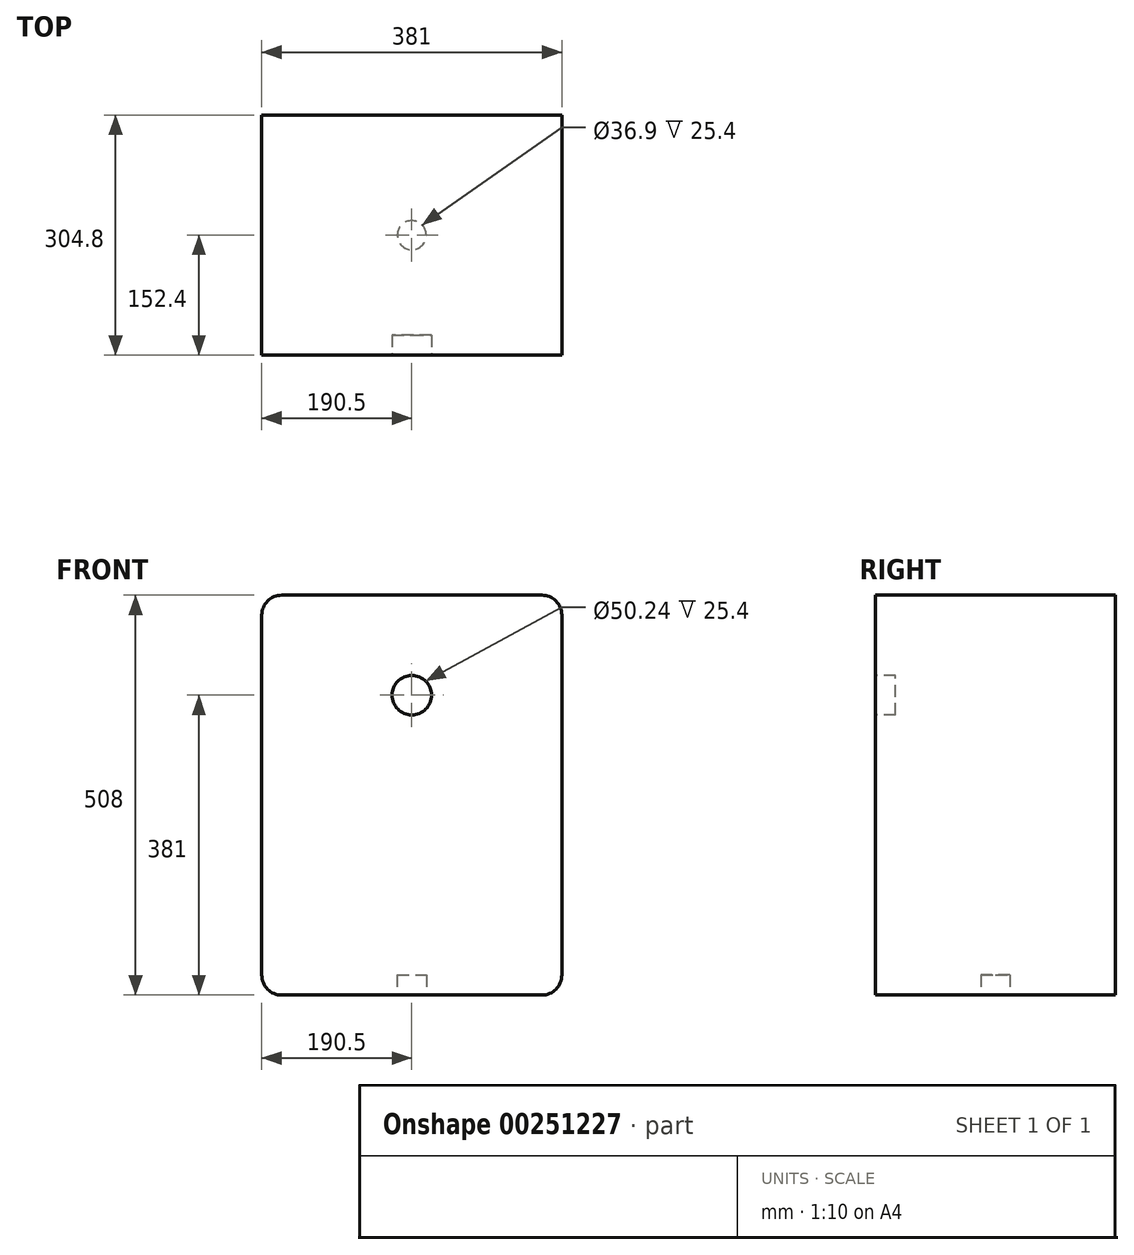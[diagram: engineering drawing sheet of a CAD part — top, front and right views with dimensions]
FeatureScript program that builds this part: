
annotation { "Feature Type Name" : "Feature", "Feature Type Description" : "" }
export const myFeature = defineFeature(function(context is Context, id is Id, definition is map)
    precondition{}
    {
        {
            var Q0;
            Q0=qCreatedBy(makeId("Front.planeOp"),FACE);
            var sketch = newSketch(context, id + "F0", { "sketchPlane" : qUnion([Q0])});
            skLineSegment(sketch, "E0.bottom", {"start": v(-190.5, 254) * mm, "end": v(190.5, 254) * mm});
            skLineSegment(sketch, "E0.top", {"start": v(-190.5, -254) * mm, "end": v(190.5, -254) * mm});
            skLineSegment(sketch, "E0.left", {"start": v(-190.5, 254) * mm, "end": v(-190.5, -254) * mm});
            skLineSegment(sketch, "E0.right", {"start": v(190.5, 254) * mm, "end": v(190.5, -254) * mm});
            skPoint(sketch, "E0.middle", {"position": v(0, 0) * mm});
            skSolve(sketch);
        }
        {
            var Q0;
            Q0=makeQuery(id+"F0.imprint","IMPRINT",FACE,{"disambiguationData":[TD([[makeQuery(id+"F0.imprint","IMPRINT",EDGE,{"derivedFrom":sQuery(id+"F0.wireOp",EDGE,"E0.bottom")}),-1.0]])]});
            extrude(context, id + "F1", {"entities" : qUnion([Q0]), "depth" : 304.8 * mm});
        }
        {
            var Q0;
            Q0=makeQuery(id+"F1.opExtrude","SWEPT_EDGE",EDGE,{"disambiguationData":[OSD([sQuery(id+"F0.wireOp",EDGE,"E0.bottom"),sQuery(id+"F0.wireOp",EDGE,"E0.left")])]});
            var Q1;
            Q1=makeQuery(id+"F1.opExtrude","SWEPT_EDGE",EDGE,{"disambiguationData":[OSD([sQuery(id+"F0.wireOp",EDGE,"E0.bottom"),sQuery(id+"F0.wireOp",EDGE,"E0.right")])]});
            var Q2;
            Q2=makeQuery(id+"F1.opExtrude","SWEPT_EDGE",EDGE,{"disambiguationData":[OSD([sQuery(id+"F0.wireOp",EDGE,"E0.top"),sQuery(id+"F0.wireOp",EDGE,"E0.right")])]});
            var Q3;
            Q3=makeQuery(id+"F1.opExtrude","SWEPT_EDGE",EDGE,{"disambiguationData":[OSD([sQuery(id+"F0.wireOp",EDGE,"E0.top"),sQuery(id+"F0.wireOp",EDGE,"E0.left")])]});
            fillet(context, id + "F2", {"entities" : qUnion([Q0, Q1, Q2, Q3]), "radius" : 25.4 * mm, "tangentPropagation" : true, "allowEdgeOverflow" : false});
        }
        {
            var Q0;
            Q0=makeQuery(id+"F1.opExtrude","SWEPT_FACE",FACE,{"disambiguationData":[OSD([sQuery(id+"F0.wireOp",EDGE,"E0.top")])]});
            var sketch = newSketch(context, id + "F3", { "sketchPlane" : qUnion([Q0])});
            skCircle(sketch, "E1", {"center": v(0, 152.4) * mm, "radius": 18.45 * mm});
            skPoint(sketch, "E1.centerSnap0", {"position": v(-165.1, 152.4) * mm});
            skPoint(sketch, "E1.centerSnap1", {"position": v(0, 304.8) * mm});
            skSolve(sketch);
        }
        {
            var Q0;
            Q0=makeQuery(id+"F3.imprint","IMPRINT",FACE,{"disambiguationData":[TD([[makeQuery(id+"F3.imprint","IMPRINT",EDGE,{"derivedFrom":sQuery(id+"F3.wireOp",EDGE,"E1")}),1.0]])]});
            extrude(context, id + "F4", {"entities" : qUnion([Q0]), "operationType" : NewBodyOperationType.REMOVE, "oppositeDirection" : true, "depth" : 25.4 * mm});
        }
        {
            var Q0;
            Q0=makeQuery(id+"F1.opExtrude","CAP_FACE",FACE,{"disambiguationData":[OSD([sQuery(id+"F0.wireOp",EDGE,"E0.bottom"),sQuery(id+"F0.wireOp",EDGE,"E0.top"),sQuery(id+"F0.wireOp",EDGE,"E0.left"),sQuery(id+"F0.wireOp",EDGE,"E0.right")])],"isStart":false});
            var sketch = newSketch(context, id + "F5", { "sketchPlane" : qUnion([Q0])});
            skSolve(sketch);
        }
        {
            var Q0;
            {var subQ3=sQuery(id+"F0.wireOp",EDGE,"E0.bottom");Q0=makeQuery(id+"F5.imprint","IMPRINT",FACE,{"disambiguationData":[TD([[makeQuery(id+"F5.imprint","IMPRINT",EDGE,{"derivedFrom":makeQuery(id+"F1.opExtrude","CAP_EDGE",EDGE,{"disambiguationData":[OSD([subQ3])],"isStart":false})}),-1.0]])]});}
            var sketch = newSketch(context, id + "F6", { "sketchPlane" : qUnion([Q0])});
            skCircle(sketch, "E2", {"center": v(0, 127) * mm, "radius": 88.9 * mm});
            skCircle(sketch, "E3", {"center": v(0, 127) * mm, "radius": 25.12 * mm});
            skSolve(sketch);
        }
        {
            var Q0;
            Q0=makeQuery(id+"F6.imprint","IMPRINT",FACE,{"disambiguationData":[TD([[makeQuery(id+"F6.imprint","IMPRINT",EDGE,{"derivedFrom":sQuery(id+"F6.wireOp",EDGE,"E3")}),1.0]])]});
            extrude(context, id + "F7", {"entities" : qUnion([Q0]), "operationType" : NewBodyOperationType.REMOVE, "oppositeDirection" : true, "depth" : 25.4 * mm});
        }
    });
